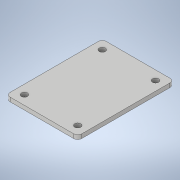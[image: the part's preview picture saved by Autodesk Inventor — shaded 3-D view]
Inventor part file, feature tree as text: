
AUTODESK INVENTOR PART (.ipt)
format: ipt  version: 2021 (Build 250183000, 183)  size: 123,392 bytes
history: native  units: mm
features: extrude x2, sketch x2, other x1, fillet x1
ambient origin geometry x8: Origin, YZ Plane, XZ Plane, XY Plane, X Axis, Y Axis, Z Axis, Center Point
bodies: Body1 (feature_tree)
feature tree (6):
  other  "Sólido1"
  extrude  "Extrusão1"  Depth=47.0mm
  fillet  "Arredondamento1"  Radius=2.0mm
  extrude  "Extrusão4"  Depth=2.0mm
  sketch  "Esboço1"  dims[d0=35.0mm d1=47.0mm d2=2.0mm d3=0.0mm]
  sketch  "Esboço5"  dims[d4=2.0mm d5=7.3mm d6=7.3mm d7=7.3mm d8=7.3mm d26=3.01mm d27=4.5mm d28=4.5mm d29=20.0mm d31=26.0mm d32=20.0mm d34=38.0mm d37=4.5mm d38=0.0mm]
